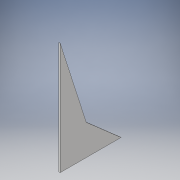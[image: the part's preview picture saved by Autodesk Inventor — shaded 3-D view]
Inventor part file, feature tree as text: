
AUTODESK INVENTOR PART (.ipt)
format: ipt  version: 2017 (Build 210142000, 142)  size: 92,672 bytes
history: native  units: in
note: dims shown in document units (in); Inventor stores cm internally (conversion verified against a paired STEP export)
features: extrude x1, sketch x1
ambient origin geometry x8: Origin, YZ Plane, XZ Plane, XY Plane, X Axis, Y Axis, Z Axis, Center Point
bodies: Solid1 (feature_tree)
feature tree (2):
  extrude  "Extrusion1"  TaperAngle=90.0deg  [1 undecoded]
  sketch  "Sketch1"  dims[d5=2.5in d6=90.0deg d7=4.6in d8=0.05in d9=0.0in]
note: 1 required parameter value undecoded (feature->parameter linkage not recoverable at this tier; creation-order binding heuristic only, values carry confidence <= 0.55)
